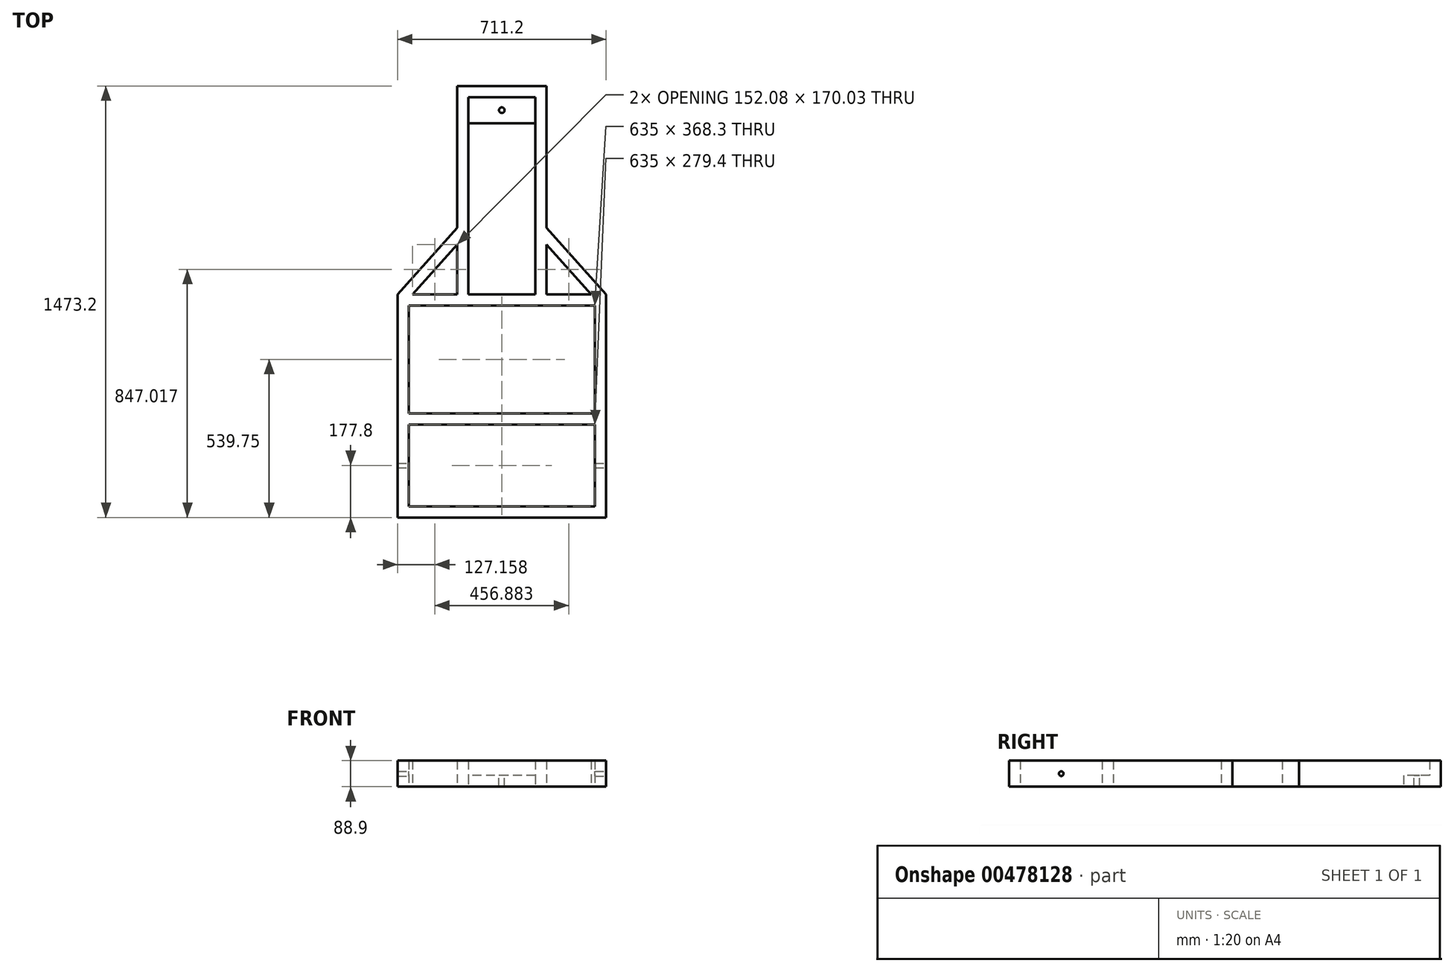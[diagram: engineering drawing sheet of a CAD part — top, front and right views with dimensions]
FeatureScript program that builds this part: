
annotation { "Feature Type Name" : "Feature", "Feature Type Description" : "" }
export const myFeature = defineFeature(function(context is Context, id is Id, definition is map)
    precondition{}
    {
        {
            var Q0;
            Q0=qCreatedBy(makeId("Top.planeOp"),FACE);
            var sketch = newSketch(context, id + "F0", { "sketchPlane" : qUnion([Q0])});
            skLineSegment(sketch, "E0.bottom", {"start": v(0, 0) * mm, "end": v(-304.8, 0) * mm});
            skLineSegment(sketch, "E0.top", {"start": v(0, -711.2) * mm, "end": v(-304.8, -711.2) * mm});
            skLineSegment(sketch, "E0.left", {"start": v(0, 0) * mm, "end": v(0, -711.2) * mm});
            skLineSegment(sketch, "E0.right", {"start": v(-304.8, 0) * mm, "end": v(-304.8, -711.2) * mm});
            skLineSegment(sketch, "E1", {"start": v(-152.4, -711.2) * mm, "end": v(-508, -711.2) * mm});
            skLineSegment(sketch, "E2.bottom", {"start": v(-508, -711.2) * mm, "end": v(203.2, -711.2) * mm});
            skLineSegment(sketch, "E2.top", {"start": v(-508, -1473.2) * mm, "end": v(203.2, -1473.2) * mm});
            skLineSegment(sketch, "E2.left", {"start": v(-508, -711.2) * mm, "end": v(-508, -1473.2) * mm});
            skLineSegment(sketch, "E2.right", {"start": v(203.2, -711.2) * mm, "end": v(203.2, -1473.2) * mm});
            skLineSegment(sketch, "E3.0", {"start": v(-508, -1117.6) * mm, "end": v(203.2, -1117.6) * mm});
            skLineSegment(sketch, "E4.0", {"start": v(-469.9, -749.3) * mm, "end": v(-469.9, -1435.1) * mm});
            skLineSegment(sketch, "E4.1", {"start": v(-469.9, -749.3) * mm, "end": v(165.1, -749.3) * mm});
            skLineSegment(sketch, "E4.2", {"start": v(165.1, -749.3) * mm, "end": v(165.1, -1435.1) * mm});
            skLineSegment(sketch, "E4.3", {"start": v(-469.9, -1435.1) * mm, "end": v(165.1, -1435.1) * mm});
            skLineSegment(sketch, "E5.0", {"start": v(-508, -1155.7) * mm, "end": v(203.2, -1155.7) * mm});
            skLineSegment(sketch, "E6", {"start": v(-508, -711.2) * mm, "end": v(-304.8, -484.02) * mm});
            skLineSegment(sketch, "E7", {"start": v(203.2, -711.2) * mm, "end": v(0, -484.02) * mm});
            skLineSegment(sketch, "E8.0", {"start": v(174.8, -736.6) * mm, "end": v(-28.4, -509.42) * mm});
            skLineSegment(sketch, "E9.0", {"start": v(-479.6, -736.6) * mm, "end": v(-276.4, -509.42) * mm});
            skLineSegment(sketch, "E10.0", {"start": v(-266.7, -38.1) * mm, "end": v(-266.7, -711.2) * mm});
            skLineSegment(sketch, "E10.1", {"start": v(-38.1, -38.1) * mm, "end": v(-266.7, -38.1) * mm});
            skLineSegment(sketch, "E10.2", {"start": v(-38.1, -38.1) * mm, "end": v(-38.1, -711.2) * mm});
            skLineSegment(sketch, "E11.0", {"start": v(-38.1, -127) * mm, "end": v(-266.7, -127) * mm});
            skSolve(sketch);
        }
        {
            var Q0;
            {var subQ6=sQuery(id+"F0.wireOp",EDGE,"E0.bottom");Q0=makeQuery(id+"F0.imprint","IMPRINT",FACE,{"disambiguationData":[TD([[makeQuery(id+"F0.imprint","IMPRINT",EDGE,{"derivedFrom":subQ6}),1.0]])]});}
            var Q1;
            {var subQ0=sQuery(id+"F0.wireOp",EDGE,"E6");Q1=makeQuery(id+"F0.imprint","IMPRINT",FACE,{"disambiguationData":[TD([[makeQuery(id+"F0.imprint","IMPRINT",EDGE,{"derivedFrom":subQ0}),-1.0]])]});}
            var Q2;
            {var subQ0=sQuery(id+"F0.wireOp",EDGE,"E7");Q2=makeQuery(id+"F0.imprint","IMPRINT",FACE,{"disambiguationData":[TD([[makeQuery(id+"F0.imprint","IMPRINT",EDGE,{"derivedFrom":subQ0}),1.0]])]});}
            var Q3;
            {var subQ19=sQuery(id+"F0.wireOp",EDGE,"E4.1");Q3=makeQuery(id+"F0.imprint","IMPRINT",FACE,{"disambiguationData":[TD([[makeQuery(id+"F0.imprint","IMPRINT",EDGE,{"derivedFrom":subQ19}),1.0]])]});}
            var Q4;
            {var subQ0=sQuery(id+"F0.wireOp",EDGE,"E4.0");var subQ1=sQuery(id+"F0.wireOp",EDGE,"E3.0");var subQ2=makeQuery(id+"F0.imprint","INTERSECT",VERTEX,{"derivedFrom":[subQ1,subQ0]});Q4=makeQuery(id+"F0.imprint","IMPRINT",FACE,{"disambiguationData":[TD([[makeQuery(id+"F0.imprint","IMPRINT",EDGE,{"disambiguationData":[TD([[subQ2,-1.0]])],"derivedFrom":subQ1}),-1.0]])]});}
            var Q5;
            {var subQ0=sQuery(id+"F0.wireOp",EDGE,"E3.0");var subQ1=sQuery(id+"F0.wireOp",EDGE,"E2.right");var subQ2=makeQuery(id+"F0.imprint","INTERSECT",VERTEX,{"derivedFrom":[subQ1,subQ0]});Q5=makeQuery(id+"F0.imprint","IMPRINT",FACE,{"disambiguationData":[TD([[makeQuery(id+"F0.imprint","IMPRINT",EDGE,{"disambiguationData":[TD([[subQ2,-1.0]])],"derivedFrom":subQ1}),-1.0]])]});}
            var Q6;
            {var subQ5=sQuery(id+"F0.wireOp",EDGE,"E2.top");Q6=makeQuery(id+"F0.imprint","IMPRINT",FACE,{"disambiguationData":[TD([[makeQuery(id+"F0.imprint","IMPRINT",EDGE,{"derivedFrom":subQ5}),1.0]])]});}
            var Q7;
            {var subQ0=sQuery(id+"F0.wireOp",EDGE,"E3.0");var subQ1=sQuery(id+"F0.wireOp",EDGE,"E2.left");var subQ2=makeQuery(id+"F0.imprint","INTERSECT",VERTEX,{"derivedFrom":[subQ1,subQ0]});Q7=makeQuery(id+"F0.imprint","IMPRINT",FACE,{"disambiguationData":[TD([[makeQuery(id+"F0.imprint","IMPRINT",EDGE,{"disambiguationData":[TD([[subQ2,-1.0]])],"derivedFrom":subQ1}),1.0]])]});}
            extrude(context, id + "F1", {"entities" : qUnion([Q0, Q1, Q2, Q3, Q4, Q5, Q6, Q7]), "depth" : 88.9 * mm, "offsetDistance" : 25.4 * mm});
        }
        {
            var Q0;
            {var subQ0=sQuery(id+"F0.wireOp",EDGE,"E10.1");Q0=makeQuery(id+"F0.imprint","IMPRINT",FACE,{"disambiguationData":[TD([[makeQuery(id+"F0.imprint","IMPRINT",EDGE,{"derivedFrom":subQ0}),1.0]])]});}
            extrude(context, id + "F2", {"entities" : qUnion([Q0]), "operationType" : NewBodyOperationType.ADD, "depth" : 38.1 * mm, "offsetDistance" : 25.4 * mm});
        }
        {
            var Q0;
            Q0=makeQuery(id+"F2.opExtrude","CAP_FACE",FACE,{"disambiguationData":[OSD([sQuery(id+"F0.wireOp",EDGE,"E10.0"),sQuery(id+"F0.wireOp",EDGE,"E10.1"),sQuery(id+"F0.wireOp",EDGE,"E10.2"),sQuery(id+"F0.wireOp",EDGE,"E11.0")])],"isStart":false});
            var sketch = newSketch(context, id + "F3", { "sketchPlane" : qUnion([Q0])});
            skLineSegment(sketch, "E12", {"start": v(-266.7, -38.1) * mm, "end": v(-38.1, -127) * mm, "construction": true});
            skCircle(sketch, "E13", {"center": v(-152.4, -82.55) * mm, "radius": 9.53 * mm});
            skSolve(sketch);
        }
        {
            var Q0;
            Q0=makeQuery(id+"F3.imprint","IMPRINT",FACE,{"disambiguationData":[TD([[makeQuery(id+"F3.imprint","IMPRINT",EDGE,{"derivedFrom":sQuery(id+"F3.wireOp",EDGE,"E13")}),1.0]])]});
            var Q1;
            Q1=sQuery(id+"F3.wireOp",EDGE,"E13");
            extrude(context, id + "F4", {"entities" : qUnion([Q0]), "operationType" : NewBodyOperationType.REMOVE, "surfaceEntities" : qUnion([Q1]), "endBound" : BoundingType.THROUGH_ALL, "oppositeDirection" : true, "depth" : 25.4 * mm, "offsetDistance" : 25.4 * mm});
        }
        {
            var Q0;
            {var subQ0=sQuery(id+"F0.wireOp",EDGE,"E4.2");Q0=makeQuery(id+"F1.opExtrude","SWEPT_FACE",FACE,{"disambiguationData":[OSD([subQ0]),TDD([makeQuery(id+"F0.imprint","IMPRINT",EDGE,{"disambiguationData":[TD([[makeQuery(id+"F0.imprint","INTERSECT",VERTEX,{"derivedFrom":[subQ0,sQuery(id+"F0.wireOp",EDGE,"E4.3")]}),1.0]])],"derivedFrom":subQ0})])]});}
            var sketch = newSketch(context, id + "F5", { "sketchPlane" : qUnion([Q0])});
            skLineSegment(sketch, "E14", {"start": v(1155.7, 0) * mm, "end": v(1435.1, 88.9) * mm, "construction": true});
            skCircle(sketch, "E15", {"center": v(1295.4, 44.45) * mm, "radius": 7.94 * mm});
            skSolve(sketch);
        }
        {
            var Q0;
            Q0=makeQuery(id+"F5.imprint","IMPRINT",FACE,{"disambiguationData":[TD([[makeQuery(id+"F5.imprint","IMPRINT",EDGE,{"derivedFrom":sQuery(id+"F5.wireOp",EDGE,"E15")}),1.0]])]});
            extrude(context, id + "F6", {"entities" : qUnion([Q0]), "operationType" : NewBodyOperationType.REMOVE, "endBound" : BoundingType.THROUGH_ALL, "depth" : 25.4 * mm, "offsetDistance" : 25.4 * mm, "hasSecondDirection" : true, "secondDirectionBound" : BoundingType.THROUGH_ALL, "secondDirectionOppositeDirection" : true, "secondDirectionDepth" : 25.4 * mm});
        }
    });
